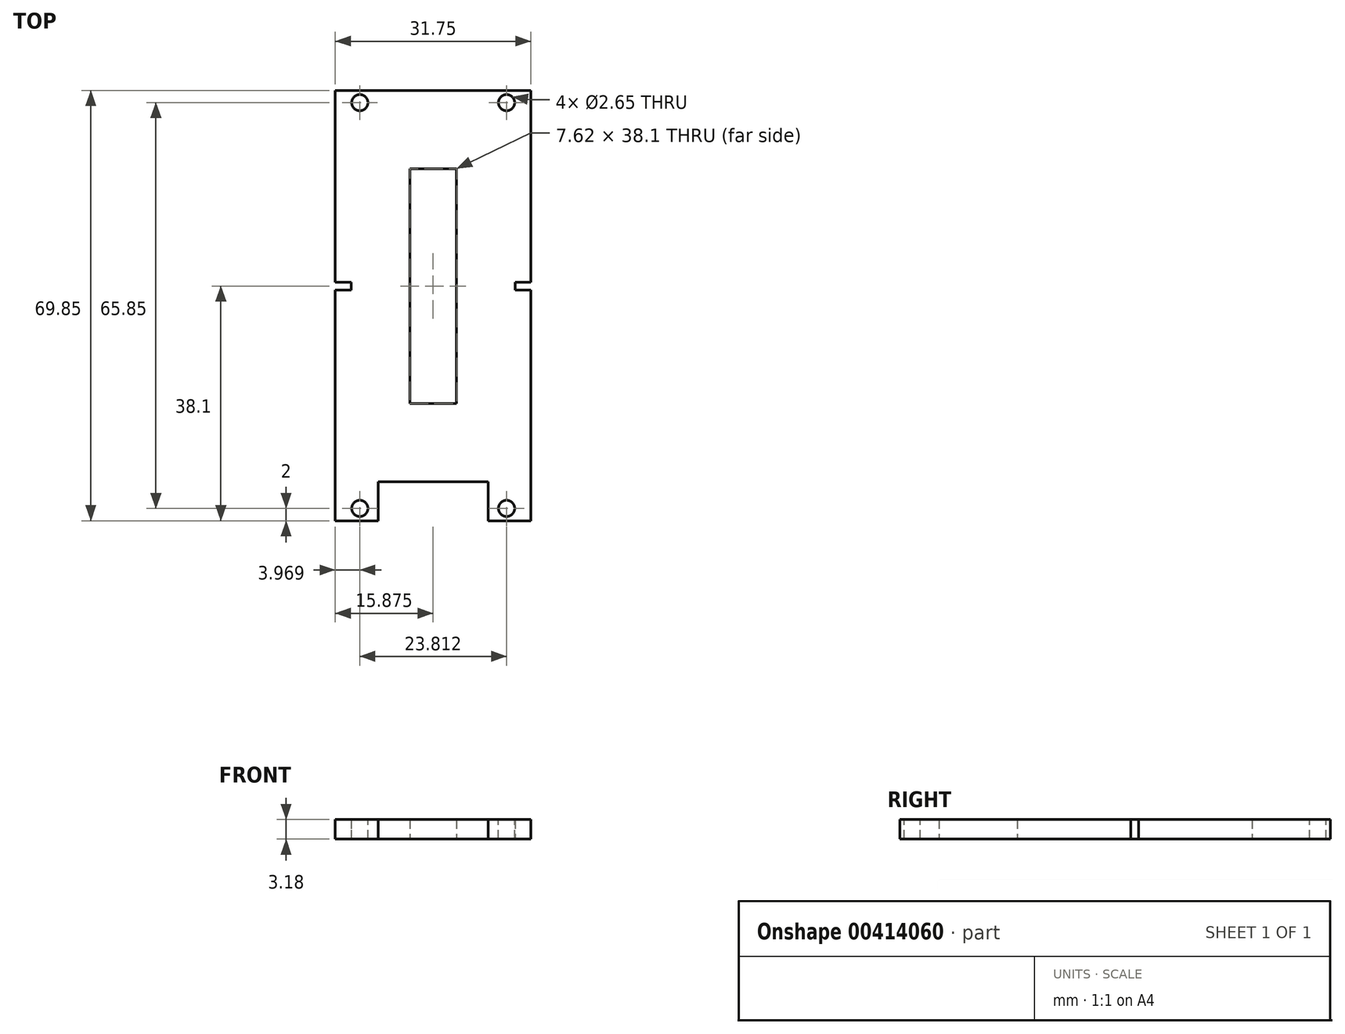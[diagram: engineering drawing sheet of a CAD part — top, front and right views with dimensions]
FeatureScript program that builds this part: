
annotation { "Feature Type Name" : "Feature", "Feature Type Description" : "" }
export const myFeature = defineFeature(function(context is Context, id is Id, definition is map)
    precondition{}
    {
        {
            var Q0;
            Q0=qCreatedBy(makeId("Top.planeOp"),FACE);
            var sketch = newSketch(context, id + "F0", { "sketchPlane" : qUnion([Q0])});
            skLineSegment(sketch, "E0.bottom", {"start": v(0, 0) * mm, "end": v(31.75, 0) * mm});
            skLineSegment(sketch, "E0.top", {"start": v(0, 63.5) * mm, "end": v(31.75, 63.5) * mm});
            skLineSegment(sketch, "E0.left", {"start": v(0, 0) * mm, "end": v(0, 63.5) * mm});
            skLineSegment(sketch, "E0.right", {"start": v(31.75, 0) * mm, "end": v(31.75, 63.5) * mm});
            skLineSegment(sketch, "E1", {"start": v(15.87, 63.5) * mm, "end": v(15.88, 0) * mm});
            skLineSegment(sketch, "E2.bottom", {"start": v(19.68, 50.8) * mm, "end": v(12.06, 50.8) * mm});
            skLineSegment(sketch, "E2.top", {"start": v(19.68, 12.7) * mm, "end": v(12.06, 12.7) * mm});
            skLineSegment(sketch, "E2.left", {"start": v(19.68, 50.8) * mm, "end": v(19.68, 12.7) * mm});
            skLineSegment(sketch, "E2.right", {"start": v(12.06, 50.8) * mm, "end": v(12.06, 12.7) * mm});
            skPoint(sketch, "E2.middle", {"position": v(15.87, 31.75) * mm});
            skSolve(sketch);
        }
        {
            var Q0;
            Q0=makeQuery(id+"F0.imprint","IMPRINT",FACE,{"disambiguationData":[TD([[makeQuery(id+"F0.imprint","IMPRINT",EDGE,{"derivedFrom":sQuery(id+"F0.wireOp",EDGE,"E0.bottom")}),1.0]])]});
            extrude(context, id + "F1", {"entities" : qUnion([Q0]), "depth" : 3.17 * mm});
        }
        {
            var Q0;
            Q0=makeQuery(id+"F1.opExtrude","SWEPT_FACE",FACE,{"disambiguationData":[OSD([sQuery(id+"F0.wireOp",EDGE,"E0.right")])]});
            var sketch = newSketch(context, id + "F2", { "sketchPlane" : qUnion([Q0])});
            skLineSegment(sketch, "E3.bottom", {"start": v(32.38, 3.18) * mm, "end": v(31.12, 3.18) * mm});
            skLineSegment(sketch, "E3.top", {"start": v(32.38, 0) * mm, "end": v(31.12, 0) * mm});
            skLineSegment(sketch, "E3.left", {"start": v(32.38, 3.18) * mm, "end": v(32.38, 0) * mm});
            skLineSegment(sketch, "E3.right", {"start": v(31.12, 3.18) * mm, "end": v(31.12, 0) * mm});
            skPoint(sketch, "E3.middle", {"position": v(31.75, 1.59) * mm});
            skPoint(sketch, "E4.orphan", {"position": v(31.75, 3.18) * mm});
            skPoint(sketch, "E5.end.orphan", {"position": v(31.75, 0) * mm});
            skSolve(sketch);
        }
        {
            var Q0;
            Q0=makeQuery(id+"F2.imprint","IMPRINT",FACE,{"disambiguationData":[TD([[makeQuery(id+"F2.imprint","IMPRINT",EDGE,{"derivedFrom":sQuery(id+"F2.wireOp",EDGE,"E3.bottom")}),-1.0]])]});
            extrude(context, id + "F3", {"entities" : qUnion([Q0]), "operationType" : NewBodyOperationType.REMOVE, "oppositeDirection" : true, "depth" : 2.54 * mm});
        }
        {
            var Q0;
            Q0=makeQuery(id+"F1.opExtrude","SWEPT_FACE",FACE,{"disambiguationData":[OSD([sQuery(id+"F0.wireOp",EDGE,"E0.left")])]});
            var sketch = newSketch(context, id + "F4", { "sketchPlane" : qUnion([Q0])});
            skLineSegment(sketch, "E6.bottom", {"start": v(-31.11, 3.18) * mm, "end": v(-32.38, 3.18) * mm});
            skLineSegment(sketch, "E6.top", {"start": v(-31.11, 0) * mm, "end": v(-32.38, 0) * mm});
            skLineSegment(sketch, "E6.left", {"start": v(-31.11, 3.18) * mm, "end": v(-31.11, 0) * mm});
            skLineSegment(sketch, "E6.right", {"start": v(-32.38, 3.18) * mm, "end": v(-32.38, 0) * mm});
            skPoint(sketch, "E6.middle", {"position": v(-31.75, 1.59) * mm});
            skPoint(sketch, "E7.orphan", {"position": v(-31.75, 3.18) * mm});
            skPoint(sketch, "E8.end.orphan", {"position": v(-31.75, 0) * mm});
            skSolve(sketch);
        }
        {
            var Q0;
            Q0=makeQuery(id+"F4.imprint","IMPRINT",FACE,{"disambiguationData":[TD([[makeQuery(id+"F4.imprint","IMPRINT",EDGE,{"derivedFrom":sQuery(id+"F4.wireOp",EDGE,"E6.bottom")}),1.0]])]});
            extrude(context, id + "F5", {"entities" : qUnion([Q0]), "operationType" : NewBodyOperationType.REMOVE, "oppositeDirection" : true, "depth" : 2.54 * mm});
        }
        {
            var Q0;
            Q0=makeQuery(id+"F1.opExtrude","SWEPT_FACE",FACE,{"disambiguationData":[OSD([sQuery(id+"F0.wireOp",EDGE,"E0.bottom")])]});
            var sketch = newSketch(context, id + "F6", { "sketchPlane" : qUnion([Q0])});
            skLineSegment(sketch, "E9", {"start": v(15.87, 3.18) * mm, "end": v(15.87, 0) * mm});
            skLineSegment(sketch, "E10.bottom", {"start": v(24.76, 3.18) * mm, "end": v(6.98, 3.18) * mm});
            skLineSegment(sketch, "E10.top", {"start": v(24.76, 0) * mm, "end": v(6.98, 0) * mm});
            skLineSegment(sketch, "E10.left", {"start": v(24.76, 3.18) * mm, "end": v(24.76, 0) * mm});
            skLineSegment(sketch, "E10.right", {"start": v(6.98, 3.18) * mm, "end": v(6.98, 0) * mm});
            skPoint(sketch, "E10.middle", {"position": v(15.87, 1.59) * mm});
            skSolve(sketch);
        }
        {
            var Q0;
            {var subQ0=sQuery(id+"F6.wireOp",EDGE,"E10.right");Q0=makeQuery(id+"F6.imprint","IMPRINT",FACE,{"disambiguationData":[TD([[makeQuery(id+"F6.imprint","IMPRINT",EDGE,{"derivedFrom":subQ0}),-1.0]])]});}
            var Q1;
            {var subQ0=sQuery(id+"F6.wireOp",EDGE,"E10.left");Q1=makeQuery(id+"F6.imprint","IMPRINT",FACE,{"disambiguationData":[TD([[makeQuery(id+"F6.imprint","IMPRINT",EDGE,{"derivedFrom":subQ0}),1.0]])]});}
            extrude(context, id + "F7", {"entities" : qUnion([Q0, Q1]), "operationType" : NewBodyOperationType.ADD, "depth" : 6.35 * mm});
        }
        {
            var Q0;
            {var subQ0=sQuery(id+"F0.wireOp",EDGE,"E0.bottom");var subQ1=makeQuery(id+"F1.opExtrude","CAP_EDGE",EDGE,{"disambiguationData":[OSD([subQ0])],"isStart":false});var subQ2=sQuery(id+"F0.wireOp",EDGE,"E0.right");var subQ4=sQuery(id+"F0.wireOp",EDGE,"E0.left");Q0=makeQuery(id+"F7.boolean.opBoolean","MERGE",FACE,{"derivedFrom":[makeQuery(id+"F1.opExtrude","CAP_FACE",FACE,{"disambiguationData":[OSD([subQ0,sQuery(id+"F0.wireOp",EDGE,"E0.top"),subQ4,subQ2])],"isStart":false}),makeQuery(id+"F7.opExtrude","SWEPT_FACE",FACE,{"disambiguationData":[OSD([subQ0]),TDD([makeQuery(id+"F6.imprint","IMPRINT",EDGE,{"disambiguationData":[TD([[makeQuery(id+"F6.imprint","INTERSECT",VERTEX,{"derivedFrom":[makeQuery(id+"F1.opExtrude","SWEPT_EDGE",EDGE,{"disambiguationData":[OSD([subQ0,subQ4])]}),subQ1]}),-1.0]])],"derivedFrom":subQ1})])]}),makeQuery(id+"F7.opExtrude","SWEPT_FACE",FACE,{"disambiguationData":[OSD([subQ0]),TDD([makeQuery(id+"F6.imprint","IMPRINT",EDGE,{"disambiguationData":[TD([[makeQuery(id+"F6.imprint","INTERSECT",VERTEX,{"derivedFrom":[makeQuery(id+"F1.opExtrude","SWEPT_EDGE",EDGE,{"disambiguationData":[OSD([subQ0,subQ2])]}),subQ1]}),1.0]])],"derivedFrom":subQ1})])]})]});}
            var sketch = newSketch(context, id + "F8", { "sketchPlane" : qUnion([Q0])});
            skLineSegment(sketch, "E11", {"start": v(3.97, -6.35) * mm, "end": v(3.97, -4.35) * mm});
            skLineSegment(sketch, "E12", {"start": v(3.97, -4.35) * mm, "end": v(27.78, -4.35) * mm});
            skLineSegment(sketch, "E13", {"start": v(27.78, -5.68) * mm, "end": v(27.78, -6.35) * mm});
            skPoint(sketch, "E14.end.orphan", {"position": v(3.5, 0) * mm});
            skPoint(sketch, "E14.start.orphan", {"position": v(3.5, -6.35) * mm});
            skPoint(sketch, "E15.end.orphan", {"position": v(28.26, 0) * mm});
            skPoint(sketch, "E15.start.orphan", {"position": v(28.26, -6.35) * mm});
            skLineSegment(sketch, "E16", {"start": v(15.87, 0) * mm, "end": v(15.87, -4.35) * mm});
            skCircle(sketch, "E17", {"center": v(3.97, -4.35) * mm, "radius": 1.32 * mm});
            skCircle(sketch, "E18", {"center": v(27.78, -4.35) * mm, "radius": 1.32 * mm});
            skLineSegment(sketch, "E19", {"start": v(27.78, -4.35) * mm, "end": v(27.78, -3.03) * mm});
            skLineSegment(sketch, "E20", {"start": v(3.97, 61.5) * mm, "end": v(27.78, 61.5) * mm});
            skCircle(sketch, "E21", {"center": v(3.97, 61.5) * mm, "radius": 1.32 * mm});
            skCircle(sketch, "E22", {"center": v(27.78, 61.5) * mm, "radius": 1.32 * mm});
            skLineSegment(sketch, "E23.trimOffspring", {"start": v(3.97, 62.82) * mm, "end": v(3.97, 63.5) * mm});
            skSolve(sketch);
        }
        {
            var Q0;
            {var subQ0=sQuery(id+"F8.wireOp",EDGE,"E12");var subQ1=sQuery(id+"F8.wireOp",EDGE,"E11");var subQ2=makeQuery(id+"F8.imprint","INTERSECT",VERTEX,{"derivedFrom":[subQ1,subQ0]});Q0=makeQuery(id+"F8.imprint","IMPRINT",FACE,{"disambiguationData":[TD([[makeQuery(id+"F8.imprint","IMPRINT",EDGE,{"disambiguationData":[TD([[subQ2,1.0]])],"derivedFrom":subQ1}),1.0]])]});}
            var Q1;
            {var subQ0=sQuery(id+"F8.wireOp",EDGE,"E12");var subQ1=sQuery(id+"F8.wireOp",EDGE,"E11");var subQ2=makeQuery(id+"F8.imprint","INTERSECT",VERTEX,{"derivedFrom":[subQ1,subQ0]});Q1=makeQuery(id+"F8.imprint","IMPRINT",FACE,{"disambiguationData":[TD([[makeQuery(id+"F8.imprint","IMPRINT",EDGE,{"disambiguationData":[TD([[subQ2,1.0]])],"derivedFrom":subQ1}),-1.0]])]});}
            var Q2;
            {var subQ0=sQuery(id+"F8.wireOp",EDGE,"E13");var subQ1=sQuery(id+"F8.wireOp",EDGE,"E12");var subQ2=makeQuery(id+"F8.imprint","INTERSECT",VERTEX,{"derivedFrom":[subQ1,subQ0]});Q2=makeQuery(id+"F8.imprint","IMPRINT",FACE,{"disambiguationData":[TD([[makeQuery(id+"F8.imprint","IMPRINT",EDGE,{"disambiguationData":[TD([[subQ2,1.0]])],"derivedFrom":subQ1}),1.0]])]});}
            var Q3;
            {var subQ0=sQuery(id+"F8.wireOp",EDGE,"E13");var subQ1=sQuery(id+"F8.wireOp",EDGE,"E12");var subQ2=makeQuery(id+"F8.imprint","INTERSECT",VERTEX,{"derivedFrom":[subQ1,subQ0]});Q3=makeQuery(id+"F8.imprint","IMPRINT",FACE,{"disambiguationData":[TD([[makeQuery(id+"F8.imprint","IMPRINT",EDGE,{"disambiguationData":[TD([[subQ2,1.0]])],"derivedFrom":subQ1}),-1.0]])]});}
            extrude(context, id + "F9", {"entities" : qUnion([Q0, Q1, Q2, Q3]), "operationType" : NewBodyOperationType.REMOVE, "oppositeDirection" : true, "depth" : 25.4 * mm});
        }
        {
            var Q0;
            {var subQ0=sQuery(id+"F8.wireOp",EDGE,"E19");Q0=makeQuery(id+"F8.imprint","IMPRINT",FACE,{"disambiguationData":[TD([[makeQuery(id+"F8.imprint","IMPRINT",EDGE,{"derivedFrom":subQ0}),-1.0]])]});}
            var Q1;
            Q1=makeQuery(id+"F8.imprint","IMPRINT",FACE,{"disambiguationData":[TD([[makeQuery(id+"F8.imprint","IMPRINT",EDGE,{"derivedFrom":sQuery(id+"F8.wireOp",EDGE,"E22")}),1.0]])]});
            var Q2;
            {var subQ0=sQuery(id+"F8.wireOp",EDGE,"E21");var subQ1=makeQuery(id+"F8.imprint","IMPRINT",VERTEX,{"disambiguationData":[OD(0.0)],"derivedFrom":subQ0});Q2=makeQuery(id+"F8.imprint","IMPRINT",FACE,{"disambiguationData":[TD([[makeQuery(id+"F8.imprint","IMPRINT",EDGE,{"disambiguationData":[TD([[subQ1,1.0]])],"derivedFrom":subQ0}),1.0]])]});}
            extrude(context, id + "F10", {"entities" : qUnion([Q0, Q1, Q2]), "operationType" : NewBodyOperationType.REMOVE, "oppositeDirection" : true, "depth" : 25.4 * mm});
        }
    });
